# Revit family: Plumbing_Drainage_hansgrohe_56271XXX-RainDrain-Go-Complete-set-shower-drain-600_NEW
name_source: partatom
category: Plumbing Fixtures
units: mm (PartAtom-declared; Revit-internal decimal feet)

## family parameters
Cut with Voids When Loaded = No
Host = Face
Maintain Annotation Orientation = No
OmniClass Number = 23.31.17.29
OmniClass Title = Shower Drains
Part Type = Normal
Room Calculation Point = No
Round Connector Dimension = Use Diameter
Shared = No

## types (4) — shared parameters
Default Elevation = 1219 mm
Description = RainDrain Go Complete set shower drain 600 tileable rear cover standard/flat installation
Manufacturer = Hansgrohe
Material 2 = Hansgrohe - Metal - Stainless Steel
Material 3 = Hansgrohe - Plastic - Black
Model = 56271XXX
Product Page URL = https://www.hansgrohe.com
Product data url = https://bimobject.com
URL = https://www.hansgrohe.com
Version = 1

## per-type parameters (varying)
| type | Connector Description | Diameter | Installation  Flat | Installation Standard | Material 1 | z_Installation 1 | z_Installation 2 |
| Installation Standard - 670 Matte Black | Water Outlet 50 mm | 50 mm | No | Yes | Hansgrohe - Metal - 670 Matte Black | 76 mm | 162 mm |
| Installation Flat - 670 Matte Black | Water Outlet 40 mm | 40 mm  [stored 0.131234 ft] | Yes | No | Hansgrohe - Metal - 670 Matte Black | 61 mm | 156 mm |
| Installation Flat - 800 Stainless Steel Optic | Water Outlet 40 mm | 40 mm  [stored 0.131234 ft] | Yes | No | Hansgrohe - Metal - 800 Stainless Steel Optic | 61 mm | 156 mm |
| Installation Standard - 800 Stainless Steel Optic | Water Outlet 50 mm | 50 mm | No | Yes | Hansgrohe - Metal - 800 Stainless Steel Optic | 76 mm | 162 mm |

note: [stored X ft] marks values corroborated as IEEE doubles in the binary element streams (Revit-internal decimal feet)

## geometry (parser evidence)
native form markers: Sweep x2
no freeform markers — native parametric forms only
